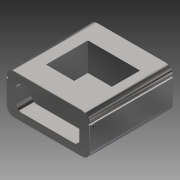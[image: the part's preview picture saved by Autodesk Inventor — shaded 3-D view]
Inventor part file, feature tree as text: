
AUTODESK INVENTOR PART (.ipt)
format: ipt  version: 2015 (Build 190159000, 159)  size: 282,112 bytes
history: native  units: in
note: dims shown in document units (in); Inventor stores cm internally (conversion verified against a paired STEP export)
features: sketch x7, extrude x6, chamfer x4, emboss x1
ambient origin geometry x8: Origin, YZ Plane, XZ Plane, XY Plane, X Axis, Y Axis, Z Axis, Center Point
bodies: Solid1 (feature_tree)
feature tree (18):
  extrude  "Extrusion1"  Depth=3.17in
  extrude  "Extrusion2"  Depth=0.3in
  extrude  "Extrusion3"  Depth=3.17in TaperAngle=0.0deg
  extrude  "Extrusion4"  Depth=2.4in
  extrude  "Extrusion5"  Depth=0.2in
  emboss  "Emboss2"
  extrude  "Extrusion6"  Depth=0.57in TaperAngle=0.0deg
  chamfer  "Chamfer1"  Distance=2.5in
  chamfer  "Chamfer2"  Distance=0.57in
  chamfer  "Chamfer3"  Distance=0.02in
  chamfer  "Chamfer4"  Distance=0.06in
  sketch  "Sketch1"  dims[d0=3.17in d1=1.53in]
  sketch  "Sketch2"  dims[d2=0.125in d3=0.3in]
  sketch  "Sketch4"  dims[d4=3.17in d5=0.0in d25=1.07in d26=0.0in]
  sketch  "Sketch5"  dims[d27=1.98in d39=2.4in]
  sketch  "Sketch7"  dims[d40=0.93in d41=0.2in]
  sketch  "Sketch8"  dims[d42=0.57in d43=0.0in d50=0.57in d51=0.0in]
  sketch  "Sketch9"  dims[d59=1.0in d60=2.5in d61=0.57in d62=0.0in d63=0.02in d64=0.0in d66=0.06in d67=0.0in d68=0.01in d69=0.125in d70=45.0deg d71=0.01in d72=0.125in d73=45.0deg d74=0.01in d75=0.125in d76=45.0deg d77=0.01in d78=0.125in d79=45.0deg]
